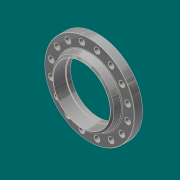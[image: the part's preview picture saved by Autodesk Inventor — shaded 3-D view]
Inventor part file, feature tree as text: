
AUTODESK INVENTOR PART (.ipt)
format: ipt  version: 2017.3 (Build 213257000, 257)  size: 303,616 bytes
history: native  units: in
note: dims shown in document units (in); Inventor stores cm internally (conversion verified against a paired STEP export)
features: chamfer x3, sketch x3, revolve x1, hole x1, pattern_circular x1, extrude x1, fillet x1
ambient origin geometry x8: Origin, YZ Plane, XZ Plane, XY Plane, X Axis, Y Axis, Z Axis, Center Point
bodies: Solid1 (feature_tree)
feature tree (11):
  revolve  "Revolution1"  [1 undecoded]
  hole  "Hole1"  [1 undecoded]
  chamfer  "Chamfer1"  Distance=14.0in
  pattern_circular  "Circular Pattern1"  [2 undecoded]
  chamfer  "Chamfer2"  Distance=14.9in
  extrude  "Extrusion1"  Depth=0.0312in
  fillet  "Fillet1"  Radius=0.4375in
  chamfer  "Chamfer3"  Distance=0.2in
  sketch  "Sketch1"  dims[d0=3.75in d1=20.5in]
  sketch  "Sketch2"  dims[d2=2.0in d3=15.0in]
  sketch  "Sketch3"  dims[d4=0.0625in d5=14.0in d6=13.0in d7=14.9in d8=0.2577in d9=0.4375in d10=0.2in d11=90.0deg d12=17.75in d13=0.0773in d14=1.25in d15=0.75in d16=0.375in d17=0.25in d18=0.5635in d19=1.0in d20=0.8108in d21=0.0625in d22=0.125in d23=45.0deg d24=6.2992in d25=360.0deg d27=0.0625in d28=0.125in d29=45.0deg d30=12.625in d31=1.0in d32=0.0in d33=0.0312in d34=0.0312in d35=0.125in d36=45.0deg]
note: 4 required parameter values undecoded (feature->parameter linkage not recoverable at this tier; creation-order binding heuristic only, values carry confidence <= 0.55)